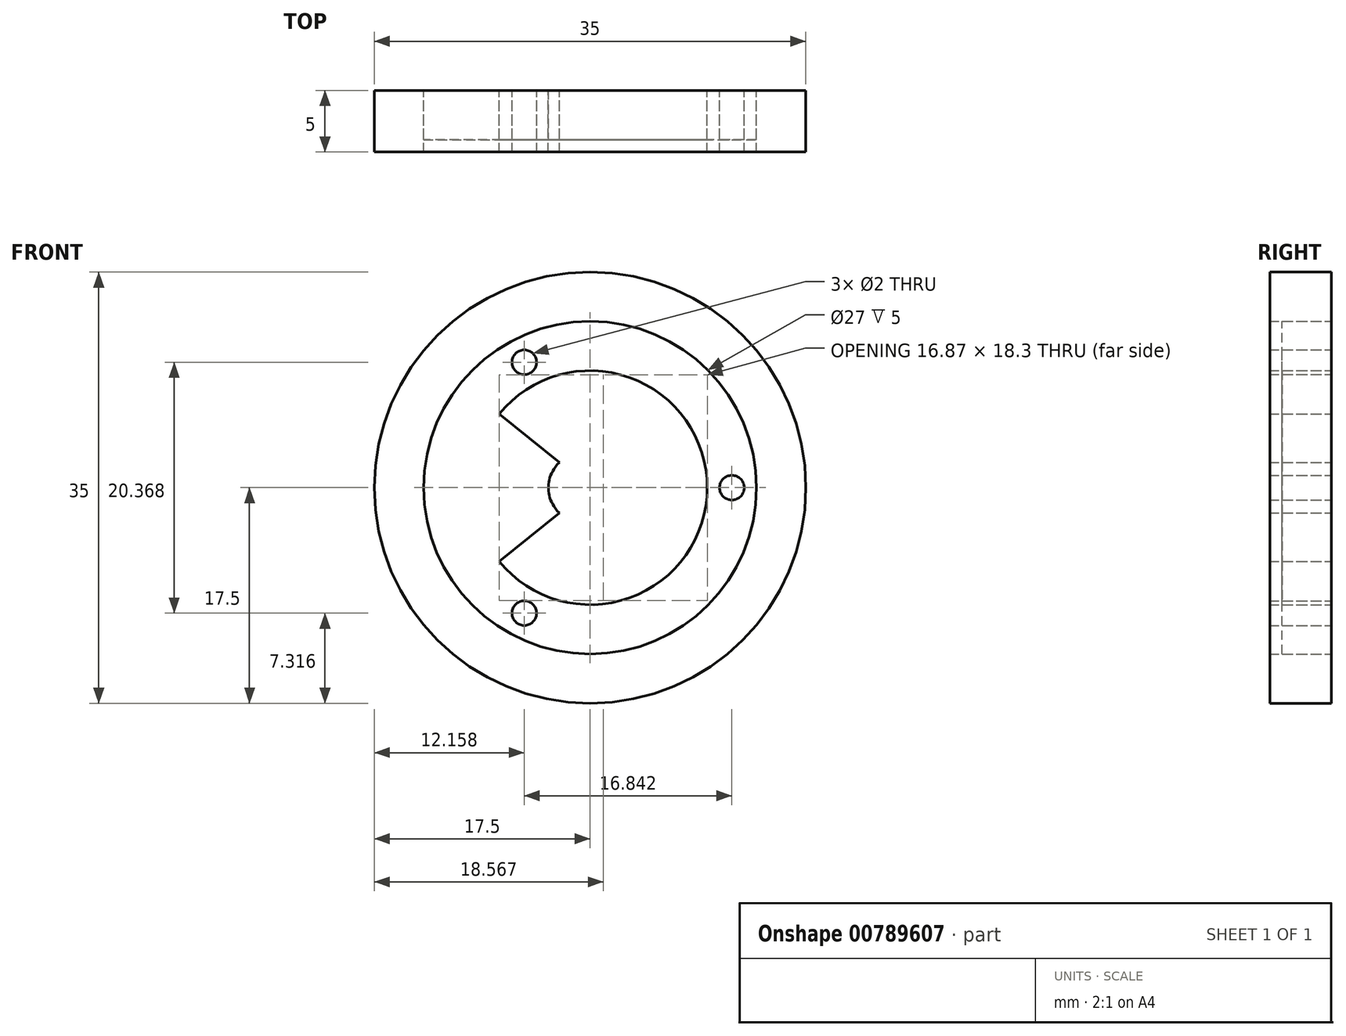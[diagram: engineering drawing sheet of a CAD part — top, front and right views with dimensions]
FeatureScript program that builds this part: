
annotation { "Feature Type Name" : "Feature", "Feature Type Description" : "" }
export const myFeature = defineFeature(function(context is Context, id is Id, definition is map)
    precondition{}
    {
        {
            var Q0;
            Q0=qCreatedBy(makeId("Front.planeOp"),FACE);
            var sketch = newSketch(context, id + "F0", { "sketchPlane" : qUnion([Q0])});
            skCircle(sketch, "E0", {"center": v(0, 0) * mm, "radius": 13.5 * mm});
            skLineSegment(sketch, "E1", {"start": v(-7.37, 6) * mm, "end": v(-2.5, 2.06) * mm});
            skLineSegment(sketch, "E2", {"start": v(-2.5, -2.06) * mm, "end": v(-7.37, -6) * mm});
            skCircle(sketch, "E3", {"center": v(-5.34, -10.18) * mm, "radius": 1 * mm});
            skCircle(sketch, "E4", {"center": v(-5.34, 10.18) * mm, "radius": 1 * mm});
            skFitSpline(sketch, "E5", {"points": [v(-2.5, 2.06) * mm, v(-3.4, 0) * mm, v(-2.5, -2.06) * mm], "startDerivative": vector(-3.94, -4.12) * mm, "endDerivative": vector(3.94, -4.12) * mm});
            skCircle(sketch, "E6", {"center": v(11.5, 0) * mm, "radius": 1 * mm});
            skPoint(sketch, "E7", {"position": v(-7.37, 6) * mm});
            skPoint(sketch, "E8", {"position": v(-7.37, -6) * mm});
            skArc(sketch, "E9", {"start": v(-7.37, 6) * mm, "mid": v(9.5, 0) * mm, "end": v(-7.37, -6) * mm});
            skCircle(sketch, "E10", {"center": v(0, 0) * mm, "radius": 17.5 * mm});
            skSolve(sketch);
        }
        {
            var Q0;
            Q0=makeQuery(id+"F0.imprint","IMPRINT",FACE,{"disambiguationData":[TD([[makeQuery(id+"F0.imprint","IMPRINT",EDGE,{"derivedFrom":sQuery(id+"F0.wireOp",EDGE,"E0")}),-1.0]])]});
            var Q1;
            Q1=makeQuery(id+"F0.imprint","IMPRINT",FACE,{"disambiguationData":[TD([[makeQuery(id+"F0.imprint","IMPRINT",EDGE,{"derivedFrom":sQuery(id+"F0.wireOp",EDGE,"E1")}),1.0]])]});
            var Q2;
            Q2=makeQuery(id+"F0.imprint","IMPRINT",FACE,{"disambiguationData":[TD([[makeQuery(id+"F0.imprint","IMPRINT",EDGE,{"derivedFrom":sQuery(id+"F0.wireOp",EDGE,"E3")}),1.0]])]});
            var Q3;
            Q3=makeQuery(id+"F0.imprint","IMPRINT",FACE,{"disambiguationData":[TD([[makeQuery(id+"F0.imprint","IMPRINT",EDGE,{"derivedFrom":sQuery(id+"F0.wireOp",EDGE,"E4")}),1.0]])]});
            var Q4;
            Q4=makeQuery(id+"F0.imprint","IMPRINT",FACE,{"disambiguationData":[TD([[makeQuery(id+"F0.imprint","IMPRINT",EDGE,{"derivedFrom":sQuery(id+"F0.wireOp",EDGE,"E6")}),1.0]])]});
            extrude(context, id + "F1", {"entities" : qUnion([Q0, Q1, Q2, Q3, Q4]), "depth" : 5 * mm, "offsetDistance" : 25 * mm});
        }
        {
            var Q0;
            Q0=makeQuery(id+"F0.imprint","IMPRINT",FACE,{"disambiguationData":[TD([[makeQuery(id+"F0.imprint","IMPRINT",EDGE,{"derivedFrom":sQuery(id+"F0.wireOp",EDGE,"E0")}),1.0]])]});
            extrude(context, id + "F2", {"entities" : qUnion([Q0]), "depth" : 4 * mm, "offsetDistance" : 25 * mm});
        }
    });
